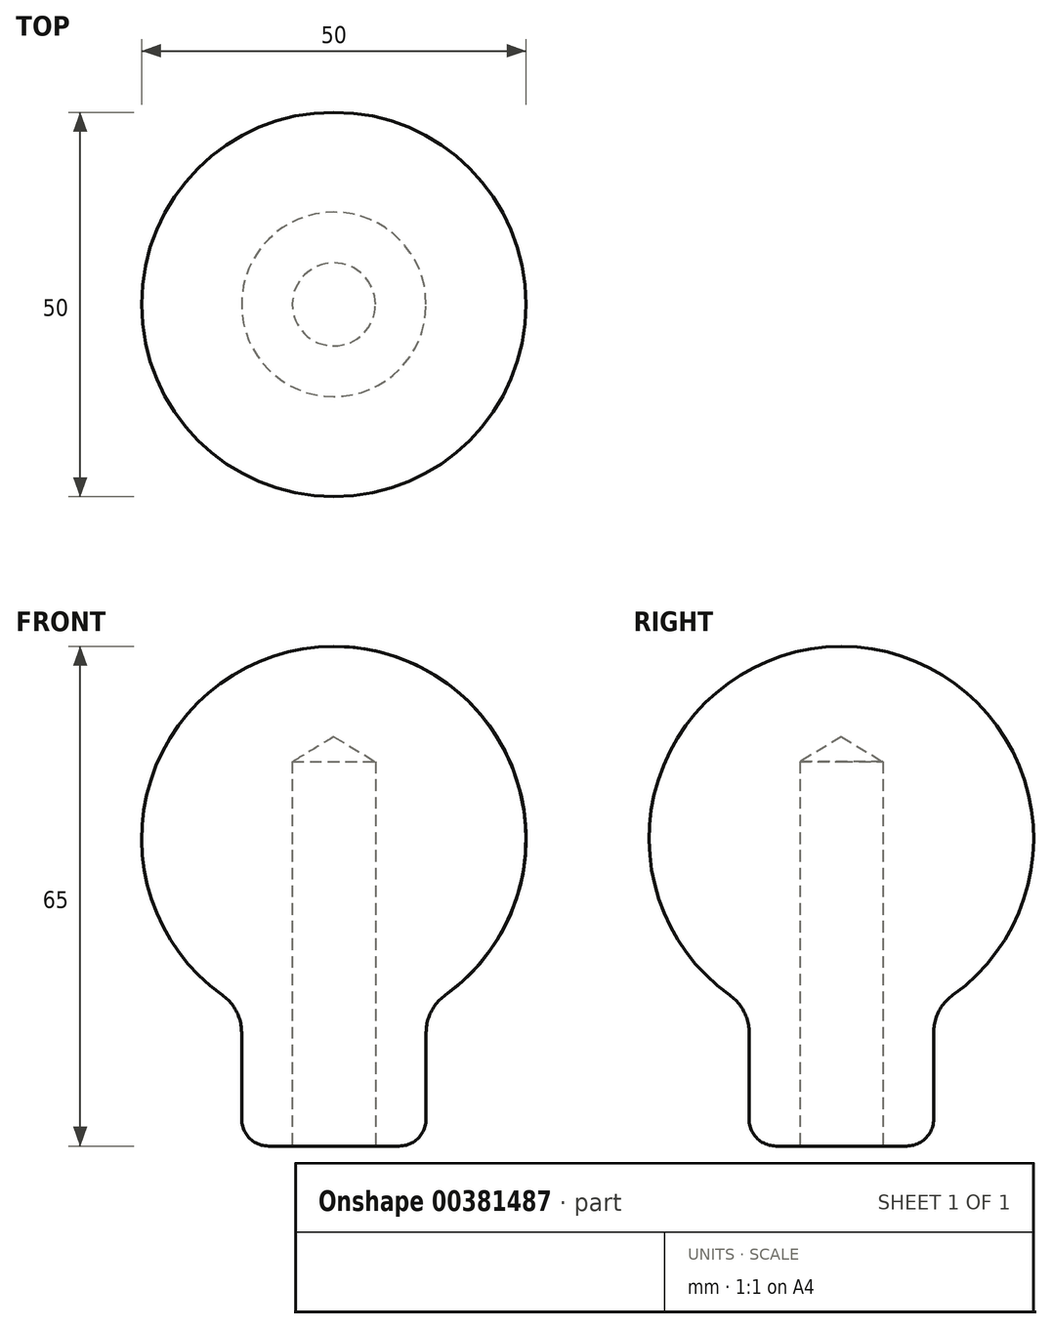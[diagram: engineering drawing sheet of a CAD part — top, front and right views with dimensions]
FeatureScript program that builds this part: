
annotation { "Feature Type Name" : "Feature", "Feature Type Description" : "" }
export const myFeature = defineFeature(function(context is Context, id is Id, definition is map)
    precondition{}
    {
        {
            var Q0;
            Q0=qCreatedBy(makeId("Front.planeOp"),FACE);
            var sketch = newSketch(context, id + "F0", { "sketchPlane" : qUnion([Q0])});
            skEllipticalArc(sketch, "E0", {});
            skLineSegment(sketch, "E1", {"start": v(0, 25) * mm, "end": v(0, -40) * mm});
            skLineSegment(sketch, "E2", {"start": v(0, -40) * mm, "end": v(-8.5, -40) * mm});
            skLineSegment(sketch, "E3", {"start": v(-12, -36.5) * mm, "end": v(-12, -25.24) * mm});
            skPoint(sketch, "E4.visualSharp", {"position": v(-12, -21.93) * mm});
            skArc(sketch, "E4.filletArc", {"start": v(-12, -25.24) * mm, "mid": v(-12.67, -22.5) * mm, "end": v(-14.52, -20.35) * mm});
            skPoint(sketch, "E5.visualSharp", {"position": v(-12, -40) * mm});
            skArc(sketch, "E5.filletArc", {"start": v(-12, -36.5) * mm, "mid": v(-10.97, -38.97) * mm, "end": v(-8.5, -40) * mm});
            const initialGuessF0  = {"E0": [0, 0, -1, 0, 0.025, 0.025, 4.71238898038469, 0.9512754309818491]};
            skSetInitialGuess(sketch, initialGuessF0);
            skSolve(sketch);
        }
        {
            var Q0;
            Q0=makeQuery(id+"F0.imprint","IMPRINT",FACE,{"disambiguationData":[TD([[makeQuery(id+"F0.imprint","IMPRINT",EDGE,{"derivedFrom":sQuery(id+"F0.wireOp",EDGE,"E0")}),1.0]])]});
            var Q1;
            Q1=sQuery(id+"F0.wireOp",EDGE,"E1");
            revolve(context, id + "F1", {"entities" : qUnion([Q0]), "axis" : qUnion([Q1]), "revolveType" : RevolveType.FULL});
        }
        {
            var Q0;
            Q0=makeQuery(id+"F1.opRevolve","SWEPT_FACE",FACE,{"disambiguationData":[OSD([sQuery(id+"F0.wireOp",EDGE,"E2")])]});
            var sketch = newSketch(context, id + "F2", { "sketchPlane" : qUnion([Q0])});
            skCircle(sketch, "E6", {"center": v(0, 0) * mm, "radius": 5.4 * mm});
            skSolve(sketch);
        }
        {
            var Q0;
            Q0=sQuery(id+"F2.wireOp",VERTEX,"E6.center");
            var Q1;
            Q1=makeQuery(id+"F1.opRevolve","SWEPT_BODY",BODY,{"disambiguationData":[OSD([sQuery(id+"F0.wireOp",EDGE,"E0"),sQuery(id+"F0.wireOp",EDGE,"E1"),sQuery(id+"F0.wireOp",EDGE,"E2"),sQuery(id+"F0.wireOp",EDGE,"E3"),sQuery(id+"F0.wireOp",EDGE,"E4.filletArc"),sQuery(id+"F0.wireOp",EDGE,"E5.filletArc")])]});
            hole(context, id + "F3", {"style" : HoleStyle.C_BORE, "endStyle" : HoleEndStyle.BLIND, "holeDiameter" : 10.8 * mm, "cBoreDiameter" : 10.8 * mm, "cBoreDepth" : 10.8 * mm, "holeDepth" : 50 * mm, "isTappedThrough" : true, "tappedDepth" : 12 * mm, "tapClearance" : 3, "startFromSketch" : true, "locations" : qUnion([Q0]), "scope" : qUnion([Q1])});
        }
    });
